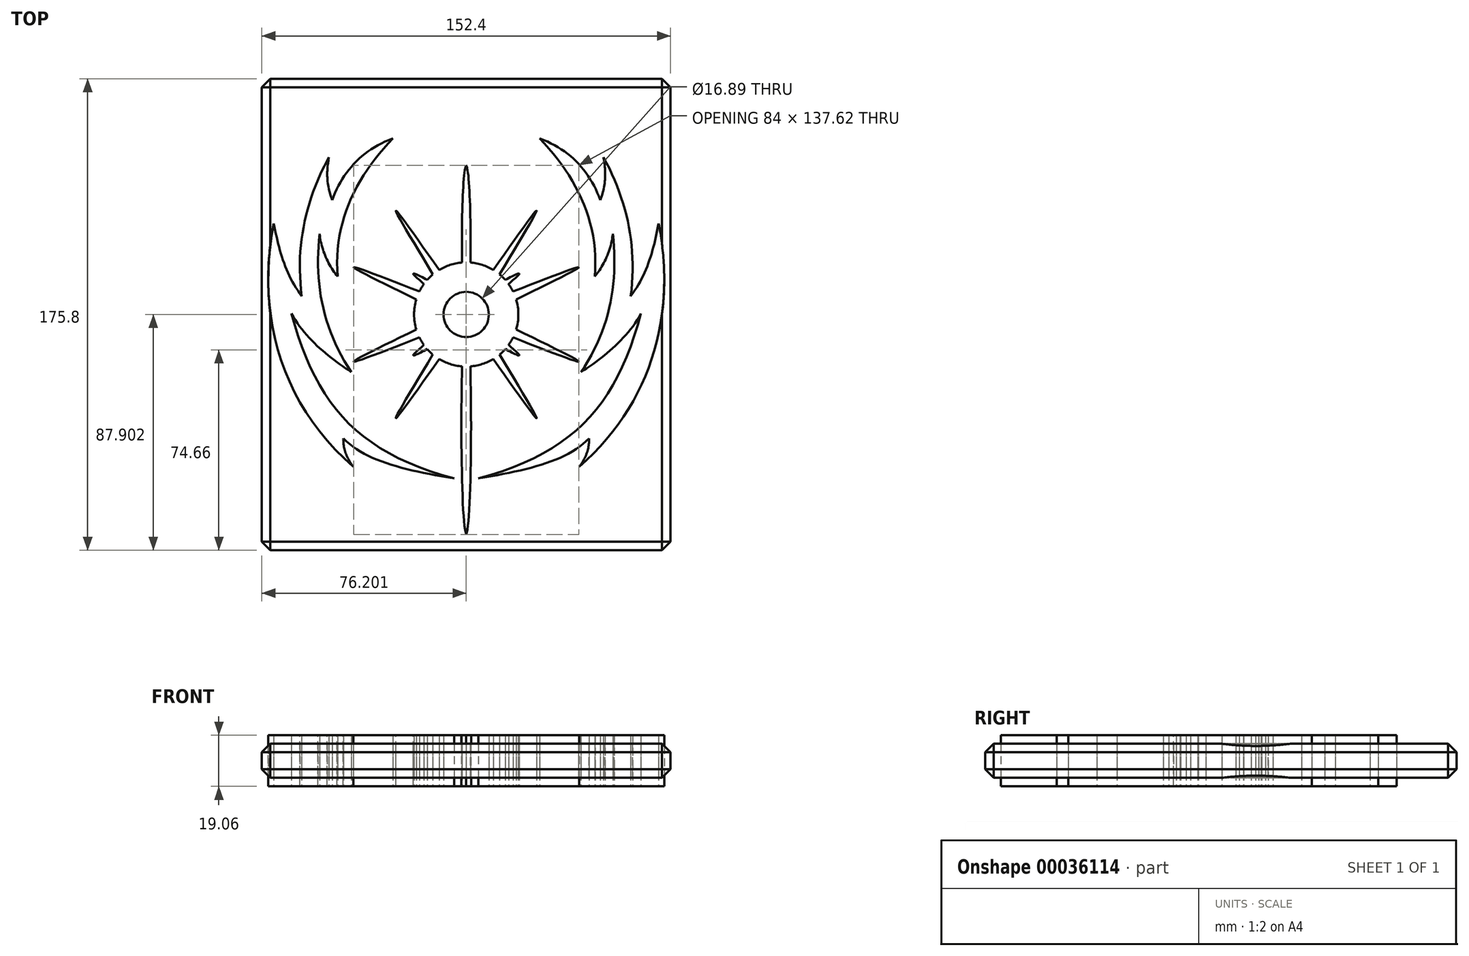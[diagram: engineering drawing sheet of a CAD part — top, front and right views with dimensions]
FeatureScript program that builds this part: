
annotation { "Feature Type Name" : "Feature", "Feature Type Description" : "" }
export const myFeature = defineFeature(function(context is Context, id is Id, definition is map)
    precondition{}
    {
        {
            var Q0;
            Q0=qCreatedBy(makeId("Top.planeOp"),FACE);
            var sketch = newSketch(context, id + "F0", { "sketchPlane" : qUnion([Q0])});
            skCircle(sketch, "E0", {"center": v(-1.85, 12.23) * mm, "radius": 8.44 * mm});
            skCircle(sketch, "E1", {"center": v(-1.85, 12.23) * mm, "radius": 19.44 * mm});
            skFitSpline(sketch, "E2", {"points": [v(16.76, 17.84) * mm, v(40.15, 29.82) * mm, v(15.6, 20.8) * mm], "startDerivative": vector(70.77, 34.48) * mm, "endDerivative": vector(-73.14, -28.59) * mm});
            skFitSpline(sketch, "E3", {"points": [v(10.59, 27.17) * mm, v(24.4, 50.95) * mm, v(8.25, 28.84) * mm], "startDerivative": vector(42.62, 70.48) * mm, "endDerivative": vector(-47.34, -67.22) * mm});
            skFitSpline(sketch, "E4", {"points": [v(13.93, 23.6) * mm, v(17.92, 27.48) * mm, v(12.69, 25.14) * mm], "startDerivative": vector(12.63, 10.93) * mm, "endDerivative": vector(-15.06, -7.8) * mm});
            skFitSpline(sketch, "E5.MirrorCS", {"points": [v(-14.28, 27.17) * mm, v(-28.1, 50.95) * mm, v(-11.95, 28.84) * mm], "startDerivative": vector(-42.62, 70.48) * mm, "endDerivative": vector(47.34, -67.22) * mm});
            skFitSpline(sketch, "E6.MirrorCS", {"points": [v(-17.62, 23.6) * mm, v(-21.62, 27.48) * mm, v(-16.38, 25.14) * mm], "startDerivative": vector(-12.63, 10.93) * mm, "endDerivative": vector(15.06, -7.8) * mm});
            skFitSpline(sketch, "E7.MirrorCS", {"points": [v(-20.46, 17.84) * mm, v(-43.85, 29.82) * mm, v(-19.3, 20.8) * mm], "startDerivative": vector(-70.77, 34.48) * mm, "endDerivative": vector(73.14, -28.59) * mm});
            skFitSpline(sketch, "E8.MirrorCS", {"points": [v(16.76, 6.63) * mm, v(40.15, -5.36) * mm, v(15.6, 3.67) * mm], "startDerivative": vector(70.77, -34.48) * mm, "endDerivative": vector(-73.14, 28.59) * mm});
            skFitSpline(sketch, "E9.MirrorCS", {"points": [v(13.93, 0.87) * mm, v(17.92, -3.01) * mm, v(12.69, -0.68) * mm], "startDerivative": vector(12.63, -10.93) * mm, "endDerivative": vector(-15.06, 7.8) * mm});
            skFitSpline(sketch, "E10.MirrorCS", {"points": [v(10.59, -2.7) * mm, v(24.4, -26.49) * mm, v(8.25, -4.38) * mm], "startDerivative": vector(42.62, -70.48) * mm, "endDerivative": vector(-47.34, 67.22) * mm});
            skFitSpline(sketch, "E11.MirrorCS", {"points": [v(-14.28, -2.7) * mm, v(-28.1, -26.49) * mm, v(-11.95, -4.38) * mm], "startDerivative": vector(-42.62, -70.48) * mm, "endDerivative": vector(47.34, 67.22) * mm});
            skFitSpline(sketch, "E12.MirrorCS", {"points": [v(-17.62, 0.87) * mm, v(-21.62, -3.01) * mm, v(-16.38, -0.68) * mm], "startDerivative": vector(-12.63, -10.93) * mm, "endDerivative": vector(15.06, 7.8) * mm});
            skFitSpline(sketch, "E13.MirrorCS", {"points": [v(-20.46, 6.63) * mm, v(-43.85, -5.36) * mm, v(-19.3, 3.67) * mm], "startDerivative": vector(-70.77, -34.48) * mm, "endDerivative": vector(73.14, 28.59) * mm});
            skFitSpline(sketch, "E14", {"points": [v(-0.3, 31.61) * mm, v(-1.85, 67.8) * mm], "startDerivative": vector(0.69, 39.8) * mm, "endDerivative": vector(-4.27, 6.76) * mm});
            skFitSpline(sketch, "E15.MirrorCS", {"points": [v(-3.4, 31.61) * mm, v(-1.85, 67.8) * mm], "startDerivative": vector(-0.69, 39.8) * mm, "endDerivative": vector(4.27, 6.76) * mm});
            skFitSpline(sketch, "E16", {"points": [v(-1.85, -69.82) * mm, v(-0.3, -7.15) * mm], "startDerivative": vector(5.53, 12.89) * mm, "endDerivative": vector(-1.6, 61.91) * mm});
            skFitSpline(sketch, "E17.MirrorCS", {"points": [v(-1.85, -69.82) * mm, v(-3.4, -7.15) * mm], "startDerivative": vector(-5.53, 12.89) * mm, "endDerivative": vector(1.6, 61.91) * mm});
            skFitSpline(sketch, "E18", {"points": [v(2.7, -48.91) * mm, v(63.3, 12.57) * mm], "startDerivative": vector(108.07, 29.1) * mm, "endDerivative": vector(27.34, 101.5) * mm});
            skFitSpline(sketch, "E19", {"points": [v(2.7, -48.91) * mm, v(43.97, -33.97) * mm], "startDerivative": vector(54.63, 9.22) * mm, "endDerivative": vector(24.86, 25.69) * mm});
            skFitSpline(sketch, "E20", {"points": [v(43.97, -33.97) * mm, v(40.25, -44.6) * mm], "startDerivative": vector(0.41, -9.53) * mm, "endDerivative": vector(-8.29, -10.36) * mm});
            skFitSpline(sketch, "E21", {"points": [v(40.25, -44.6) * mm, v(69.9, 46.18) * mm], "startDerivative": vector(81.71, 71.4) * mm, "endDerivative": vector(-19.93, 101.28) * mm});
            skFitSpline(sketch, "E22", {"points": [v(69.9, 46.18) * mm, v(59.5, 19.09) * mm], "startDerivative": vector(-5.38, -28.86) * mm, "endDerivative": vector(-17.99, -23.46) * mm});
            skFitSpline(sketch, "E23", {"points": [v(59.5, 19.09) * mm, v(49.32, 70.93) * mm], "startDerivative": vector(7.04, 56.3) * mm, "endDerivative": vector(-26.6, 49.27) * mm});
            skFitSpline(sketch, "E24", {"points": [v(49.32, 70.93) * mm, v(48.1, 54.85) * mm], "startDerivative": vector(3.14, -17.02) * mm, "endDerivative": vector(-6.52, -16.85) * mm});
            skFitSpline(sketch, "E25", {"points": [v(48.1, 54.85) * mm, v(25.56, 77.81) * mm], "startDerivative": vector(-11.3, 32.12) * mm, "endDerivative": vector(-33.63, 12.12) * mm});
            skFitSpline(sketch, "E26", {"points": [v(25.56, 77.81) * mm, v(46.07, 26.4) * mm], "startDerivative": vector(40.65, -41.98) * mm, "endDerivative": vector(-5.33, -59.86) * mm});
            skFitSpline(sketch, "E27", {"points": [v(46.07, 26.4) * mm, v(52.8, 42.31) * mm], "startDerivative": vector(10.8, 12.54) * mm, "endDerivative": vector(1.17, 16.03) * mm});
            skFitSpline(sketch, "E28", {"points": [v(52.8, 42.31) * mm, v(40.95, -9.25) * mm], "startDerivative": vector(6.2, -54.74) * mm, "endDerivative": vector(-32.62, -48.02) * mm});
            skFitSpline(sketch, "E29", {"points": [v(40.95, -9.25) * mm, v(63.3, 12.57) * mm], "startDerivative": vector(24.8, 16.18) * mm, "endDerivative": vector(15.67, 28.68) * mm});
            skFitSpline(sketch, "E30.MirrorCS", {"points": [v(-29.26, 77.81) * mm, v(-49.77, 26.4) * mm], "startDerivative": vector(-40.65, -41.98) * mm, "endDerivative": vector(5.33, -59.86) * mm});
            skFitSpline(sketch, "E31.MirrorCS", {"points": [v(-51.8, 54.85) * mm, v(-29.26, 77.81) * mm], "startDerivative": vector(11.3, 32.12) * mm, "endDerivative": vector(33.63, 12.12) * mm});
            skFitSpline(sketch, "E32.MirrorCS", {"points": [v(-53.02, 70.93) * mm, v(-51.8, 54.85) * mm], "startDerivative": vector(-3.14, -17.02) * mm, "endDerivative": vector(6.52, -16.85) * mm});
            skFitSpline(sketch, "E33.MirrorCS", {"points": [v(-63.2, 19.09) * mm, v(-53.02, 70.93) * mm], "startDerivative": vector(-7.04, 56.3) * mm, "endDerivative": vector(26.6, 49.27) * mm});
            skFitSpline(sketch, "E34.MirrorCS", {"points": [v(-73.6, 46.18) * mm, v(-63.2, 19.09) * mm], "startDerivative": vector(5.38, -28.86) * mm, "endDerivative": vector(17.99, -23.46) * mm});
            skFitSpline(sketch, "E35.MirrorCS", {"points": [v(-43.94, -44.6) * mm, v(-73.6, 46.18) * mm], "startDerivative": vector(-81.71, 71.4) * mm, "endDerivative": vector(19.93, 101.28) * mm});
            skFitSpline(sketch, "E36.MirrorCS", {"points": [v(-47.67, -33.97) * mm, v(-43.94, -44.6) * mm], "startDerivative": vector(-0.41, -9.53) * mm, "endDerivative": vector(8.29, -10.36) * mm});
            skFitSpline(sketch, "E37.MirrorCS", {"points": [v(-6.4, -48.91) * mm, v(-47.67, -33.97) * mm], "startDerivative": vector(-54.63, 9.22) * mm, "endDerivative": vector(-24.86, 25.69) * mm});
            skFitSpline(sketch, "E38.MirrorCS", {"points": [v(-6.4, -48.91) * mm, v(-67, 12.57) * mm], "startDerivative": vector(-108.07, 29.1) * mm, "endDerivative": vector(-27.34, 101.5) * mm});
            skFitSpline(sketch, "E39.MirrorCS", {"points": [v(-44.64, -9.25) * mm, v(-67, 12.57) * mm], "startDerivative": vector(-24.8, 16.18) * mm, "endDerivative": vector(-15.67, 28.68) * mm});
            skFitSpline(sketch, "E40.MirrorCS", {"points": [v(-56.5, 42.31) * mm, v(-44.64, -9.25) * mm], "startDerivative": vector(-6.2, -54.74) * mm, "endDerivative": vector(32.62, -48.02) * mm});
            skFitSpline(sketch, "E41.MirrorCS", {"points": [v(-49.77, 26.4) * mm, v(-56.5, 42.31) * mm], "startDerivative": vector(-10.8, 12.54) * mm, "endDerivative": vector(-1.17, 16.03) * mm});
            skLineSegment(sketch, "E42", {"start": v(-75.68, 55.91) * mm, "end": v(-75.68, 30.83) * mm});
            skLineSegment(sketch, "E43", {"start": v(71.98, 52.62) * mm, "end": v(71.98, 23.47) * mm});
            skLineSegment(sketch, "E44", {"start": v(74.35, 12.23) * mm, "end": v(74.35, 100.13) * mm});
            skLineSegment(sketch, "E45", {"start": v(74.35, 12.23) * mm, "end": v(74.35, -75.67) * mm});
            skLineSegment(sketch, "E46", {"start": v(74.35, -75.67) * mm, "end": v(-78.05, -75.67) * mm});
            skLineSegment(sketch, "E47", {"start": v(-78.05, -75.67) * mm, "end": v(-78.05, 100.13) * mm});
            skLineSegment(sketch, "E48", {"start": v(-78.05, 100.13) * mm, "end": v(74.35, 100.13) * mm});
            skSolve(sketch);
        }
        {
            var Q0;
            Q0=makeQuery(id+"F0.imprint","IMPRINT",FACE,{"disambiguationData":[TD([[makeQuery(id+"F0.imprint","IMPRINT",EDGE,{"derivedFrom":sQuery(id+"F0.wireOp",EDGE,"E30.MirrorCS")}),-1.0]])]});
            var Q1;
            Q1=makeQuery(id+"F0.imprint","IMPRINT",FACE,{"disambiguationData":[TD([[makeQuery(id+"F0.imprint","IMPRINT",EDGE,{"derivedFrom":sQuery(id+"F0.wireOp",EDGE,"E18")}),-1.0]])]});
            var Q2;
            Q2=makeQuery(id+"F0.imprint","IMPRINT",FACE,{"disambiguationData":[TD([[makeQuery(id+"F0.imprint","IMPRINT",EDGE,{"derivedFrom":sQuery(id+"F0.wireOp",EDGE,"E0")}),-1.0]])]});
            var Q3;
            {var subQ0=sQuery(id+"F0.wireOp",EDGE,"E2");Q3=makeQuery(id+"F0.imprint","IMPRINT",FACE,{"disambiguationData":[TD([[makeQuery(id+"F0.imprint","IMPRINT",EDGE,{"derivedFrom":subQ0}),1.0]])]});}
            var Q4;
            {var subQ0=sQuery(id+"F0.wireOp",EDGE,"E4");Q4=makeQuery(id+"F0.imprint","IMPRINT",FACE,{"disambiguationData":[TD([[makeQuery(id+"F0.imprint","IMPRINT",EDGE,{"derivedFrom":subQ0}),1.0]])]});}
            var Q5;
            {var subQ0=sQuery(id+"F0.wireOp",EDGE,"E3");Q5=makeQuery(id+"F0.imprint","IMPRINT",FACE,{"disambiguationData":[TD([[makeQuery(id+"F0.imprint","IMPRINT",EDGE,{"derivedFrom":subQ0}),1.0]])]});}
            var Q6;
            {var subQ0=sQuery(id+"F0.wireOp",EDGE,"E14");Q6=makeQuery(id+"F0.imprint","IMPRINT",FACE,{"disambiguationData":[TD([[makeQuery(id+"F0.imprint","IMPRINT",EDGE,{"derivedFrom":subQ0}),1.0]])]});}
            var Q7;
            {var subQ0=sQuery(id+"F0.wireOp",EDGE,"E5.MirrorCS");Q7=makeQuery(id+"F0.imprint","IMPRINT",FACE,{"disambiguationData":[TD([[makeQuery(id+"F0.imprint","IMPRINT",EDGE,{"derivedFrom":subQ0}),-1.0]])]});}
            var Q8;
            {var subQ0=sQuery(id+"F0.wireOp",EDGE,"E6.MirrorCS");Q8=makeQuery(id+"F0.imprint","IMPRINT",FACE,{"disambiguationData":[TD([[makeQuery(id+"F0.imprint","IMPRINT",EDGE,{"derivedFrom":subQ0}),-1.0]])]});}
            var Q9;
            {var subQ0=sQuery(id+"F0.wireOp",EDGE,"E7.MirrorCS");Q9=makeQuery(id+"F0.imprint","IMPRINT",FACE,{"disambiguationData":[TD([[makeQuery(id+"F0.imprint","IMPRINT",EDGE,{"derivedFrom":subQ0}),-1.0]])]});}
            var Q10;
            {var subQ0=sQuery(id+"F0.wireOp",EDGE,"E13.MirrorCS");Q10=makeQuery(id+"F0.imprint","IMPRINT",FACE,{"disambiguationData":[TD([[makeQuery(id+"F0.imprint","IMPRINT",EDGE,{"derivedFrom":subQ0}),1.0]])]});}
            var Q11;
            {var subQ0=sQuery(id+"F0.wireOp",EDGE,"E12.MirrorCS");Q11=makeQuery(id+"F0.imprint","IMPRINT",FACE,{"disambiguationData":[TD([[makeQuery(id+"F0.imprint","IMPRINT",EDGE,{"derivedFrom":subQ0}),1.0]])]});}
            var Q12;
            {var subQ0=sQuery(id+"F0.wireOp",EDGE,"E11.MirrorCS");Q12=makeQuery(id+"F0.imprint","IMPRINT",FACE,{"disambiguationData":[TD([[makeQuery(id+"F0.imprint","IMPRINT",EDGE,{"derivedFrom":subQ0}),1.0]])]});}
            var Q13;
            {var subQ1=sQuery(id+"F0.wireOp",EDGE,"E16");Q13=makeQuery(id+"F0.imprint","IMPRINT",FACE,{"disambiguationData":[TD([[makeQuery(id+"F0.imprint","IMPRINT",EDGE,{"derivedFrom":subQ1}),1.0]])]});}
            var Q14;
            {var subQ0=sQuery(id+"F0.wireOp",EDGE,"E10.MirrorCS");Q14=makeQuery(id+"F0.imprint","IMPRINT",FACE,{"disambiguationData":[TD([[makeQuery(id+"F0.imprint","IMPRINT",EDGE,{"derivedFrom":subQ0}),-1.0]])]});}
            var Q15;
            {var subQ0=sQuery(id+"F0.wireOp",EDGE,"E9.MirrorCS");Q15=makeQuery(id+"F0.imprint","IMPRINT",FACE,{"disambiguationData":[TD([[makeQuery(id+"F0.imprint","IMPRINT",EDGE,{"derivedFrom":subQ0}),-1.0]])]});}
            var Q16;
            {var subQ0=sQuery(id+"F0.wireOp",EDGE,"E8.MirrorCS");Q16=makeQuery(id+"F0.imprint","IMPRINT",FACE,{"disambiguationData":[TD([[makeQuery(id+"F0.imprint","IMPRINT",EDGE,{"derivedFrom":subQ0}),-1.0]])]});}
            extrude(context, id + "F1", {"entities" : qUnion([Q0, Q1, Q2, Q3, Q4, Q5, Q6, Q7, Q8, Q9, Q10, Q11, Q12, Q13, Q14, Q15, Q16]), "endBound" : BoundingType.SYMMETRIC, "depth" : 19.05 * mm});
        }
        {
            var Q0;
            {var subQ12=sQuery(id+"F0.wireOp",EDGE,"E2");Q0=makeQuery(id+"F0.imprint","IMPRINT",FACE,{"disambiguationData":[TD([[makeQuery(id+"F0.imprint","IMPRINT",EDGE,{"derivedFrom":subQ12}),-1.0]])]});}
            var Q1;
            Q1=makeQuery(id+"F0.imprint","IMPRINT",FACE,{"disambiguationData":[TD([[makeQuery(id+"F0.imprint","IMPRINT",EDGE,{"derivedFrom":sQuery(id+"F0.wireOp",EDGE,"E0")}),1.0]])]});
            extrude(context, id + "F2", {"entities" : qUnion([Q0, Q1]), "endBound" : BoundingType.SYMMETRIC, "depth" : 12.7 * mm});
        }
        {
            var Q0;
            Q0=makeQuery(id+"F2.opExtrude","SWEPT_FACE",FACE,{"disambiguationData":[OSD([sQuery(id+"F0.wireOp",EDGE,"E46")])]});
            var Q1;
            Q1=makeQuery(id+"F2.opExtrude","SWEPT_FACE",FACE,{"disambiguationData":[OSD([sQuery(id+"F0.wireOp",EDGE,"E47")])]});
            var Q2;
            Q2=makeQuery(id+"F2.opExtrude","SWEPT_FACE",FACE,{"disambiguationData":[OSD([sQuery(id+"F0.wireOp",EDGE,"E44"),sQuery(id+"F0.wireOp",EDGE,"E45")])]});
            var Q3;
            Q3=makeQuery(id+"F2.opExtrude","SWEPT_FACE",FACE,{"disambiguationData":[OSD([sQuery(id+"F0.wireOp",EDGE,"E48")])]});
            chamfer(context, id + "F3", {"entities" : qUnion([Q0, Q1, Q2, Q3]), "width" : 3.17 * mm, "tangentPropagation" : true});
        }
    });
